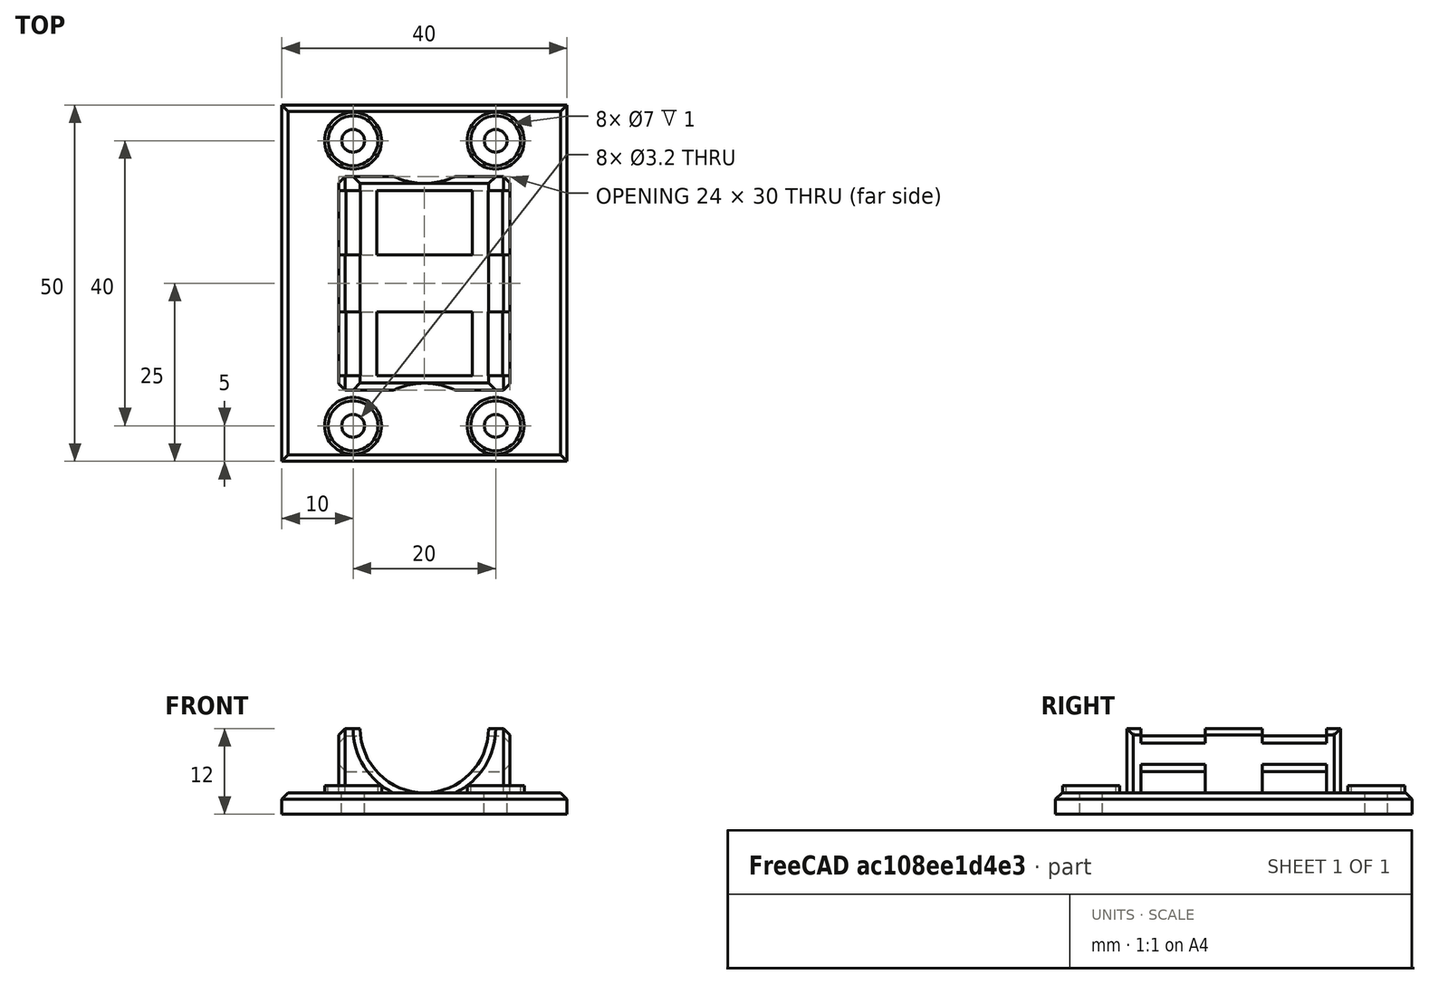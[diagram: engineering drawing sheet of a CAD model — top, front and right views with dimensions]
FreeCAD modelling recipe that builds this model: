
FCSTD DOCUMENT  (FreeCAD 0.18R14555 (Git shallow))
Label: bottom-cable-holder
License: All rights reserved
LicenseURL: http://en.wikipedia.org/wiki/All_rights_reserved
objects: Part::Cylinder×13, Part::MultiFuse×5, Part::Cut×5, Part::Box×4, Part::Chamfer×4, Part::Feature×3
note: 34 computed .brp shape members not serialized (recipe doc carries the construction recipe); baked Part::Feature solids carry a one-line shape summary decoded from their .brp

FEATURE [Part::Box] Box  label="Cube"
  AttacherType = Attacher::AttachEngine3D
  Height = 3
  Length = 40
  Width = 50
FEATURE [Part::Cylinder] Cylinder
  Angle = 360
  AttacherType = Attacher::AttachEngine3D
  Height = 1
  Placement = pos=(10,5,0) rot=(0,0,1;0rad)
  Radius = 3.5
FEATURE [Part::Cylinder] Cylinder001
  Angle = 360
  AttacherType = Attacher::AttachEngine3D
  Height = 1
  Placement = pos=(30,5,0) rot=(0,0,1;0rad)
  Radius = 3.5
FEATURE [Part::Cylinder] Cylinder002
  Angle = 360
  AttacherType = Attacher::AttachEngine3D
  Height = 1
  Placement = pos=(30,45,0) rot=(0,0,1;0rad)
  Radius = 3.5
FEATURE [Part::Cylinder] Cylinder003
  Angle = 360
  AttacherType = Attacher::AttachEngine3D
  Height = 1
  Placement = pos=(10,45,0) rot=(0,0,1;0rad)
  Radius = 3.5
FEATURE [Part::Cylinder] Cylinder004
  Angle = 360
  AttacherType = Attacher::AttachEngine3D
  Height = 4
  Placement = pos=(30,5,0) rot=(0,0,1;0rad)
  Radius = 4
FEATURE [Part::Cylinder] Cylinder005
  Angle = 360
  AttacherType = Attacher::AttachEngine3D
  Height = 4
  Placement = pos=(30,45,0) rot=(0,0,1;0rad)
  Radius = 4
FEATURE [Part::Cylinder] Cylinder006
  Angle = 360
  AttacherType = Attacher::AttachEngine3D
  Height = 4
  Placement = pos=(10,45,0) rot=(0,0,1;0rad)
  Radius = 4
FEATURE [Part::Cylinder] Cylinder007
  Angle = 360
  AttacherType = Attacher::AttachEngine3D
  Height = 4
  Placement = pos=(10,5,0) rot=(0,0,1;0rad)
  Radius = 4
FEATURE [Part::MultiFuse] Fusion
  Shapes = -> [Cylinder004,Cylinder005,Cylinder007,Cylinder006,Box]
FEATURE [Part::Cylinder] Cylinder008
  Angle = 360
  AttacherType = Attacher::AttachEngine3D
  Height = 4
  Placement = pos=(10,5,0) rot=(0,0,1;0rad)
  Radius = 1.6
FEATURE [Part::Cylinder] Cylinder009
  Angle = 360
  AttacherType = Attacher::AttachEngine3D
  Height = 4
  Placement = pos=(30,5,0) rot=(0,0,1;0rad)
  Radius = 1.6
FEATURE [Part::Cylinder] Cylinder010
  Angle = 360
  AttacherType = Attacher::AttachEngine3D
  Height = 4
  Placement = pos=(30,45,0) rot=(0,0,1;0rad)
  Radius = 1.6
FEATURE [Part::Cylinder] Cylinder011
  Angle = 360
  AttacherType = Attacher::AttachEngine3D
  Height = 4
  Placement = pos=(10,45,0) rot=(0,0,1;0rad)
  Radius = 1.6
FEATURE [Part::MultiFuse] Fusion001
  Placement = pos=(0,0,3) rot=(0,0,1;0rad)
  Shapes = -> [Cylinder,Cylinder001,Cylinder002,Cylinder003]
FEATURE [Part::Cut] Cut
  Base = -> Fusion
  Tool = -> Fusion001
FEATURE [Part::MultiFuse] Fusion002
  Shapes = -> [Cylinder011,Cylinder010,Cylinder009,Cylinder008]
FEATURE [Part::Cut] Cut001
  Base = -> Cut
  Tool = -> Fusion002
FEATURE [Part::Chamfer] Chamfer
  Base = -> Cut001
  Edges = 4 edges r=0.9: [Edge4,Edge5,Edge6,Edge7]
FEATURE [Part::Box] Box001  label="Cube001"
  AttacherType = Attacher::AttachEngine3D
  Height = 12
  Length = 24
  Placement = pos=(8,10,0) rot=(0,0,1;0rad)
  Width = 30
FEATURE [Part::Cylinder] Cylinder012
  Angle = 360
  AttacherType = Attacher::AttachEngine3D
  Height = 30
  Placement = pos=(20,10,12) rot=(-1,0,0;1.5708rad)
  Radius = 9
FEATURE [Part::Cut] Cut002
  Base = -> Box001
  Tool = -> Cylinder012
FEATURE [Part::Box] Box002  label="Cube002"
  AttacherType = Attacher::AttachEngine3D
  Height = 3
  Length = 24
  Placement = pos=(8,12,3) rot=(0,0,1;0rad)
  Width = 9
FEATURE [Part::Box] Box003  label="Cube003"
  AttacherType = Attacher::AttachEngine3D
  Height = 3
  Length = 24
  Placement = pos=(8,29,3) rot=(0,0,1;0rad)
  Width = 9
FEATURE [Part::MultiFuse] Fusion003
  Shapes = -> [Box003,Box002]
FEATURE [Part::Feature] Fusion003001  label="Fusion004"
  Placement = pos=(0,0,8) rot=(0,0,1;0rad)
  shape: bbox 24 x 26 x 3 mm, 12 faces, 2 solids (baked)
FEATURE [Part::Cut] Cut003
  Base = -> Cut002
  Tool = -> Fusion003
FEATURE [Part::Cut] Cut004
  Base = -> Cut003
  Tool = -> Fusion003001
FEATURE [Part::Chamfer] Chamfer001
  Base = -> Cut004
  Edges = 2 edges r=1: [Edge42,Edge48]
FEATURE [Part::Chamfer] Chamfer002
  Base = -> Chamfer001
  Edges = 8 edges r=1: [Edge45,Edge49,Edge55,Edge59,Edge75,Edge85,Edge94,Edge105]
FEATURE [Part::Chamfer] Chamfer003
  Base = -> Chamfer002
  Edges = 10 edges r=0.9: [Edge42,Edge44,Edge47,Edge48,Edge50,Edge78,Edge94,Edge109,Edge146,Edge150]
FEATURE [Part::MultiFuse] Fusion003002
  Shapes = -> [Chamfer003,Chamfer]
FEATURE [Part::Feature] Fusion003002001  label="Fusion003003"
  shape: bbox 40 x 50 x 12 mm, 89 faces (baked)
FEATURE [Part::Feature] Fusion003002001_solid  label="Fusion003003 (Solid)"
  shape: bbox 40 x 50 x 12 mm, 89 faces (baked)
